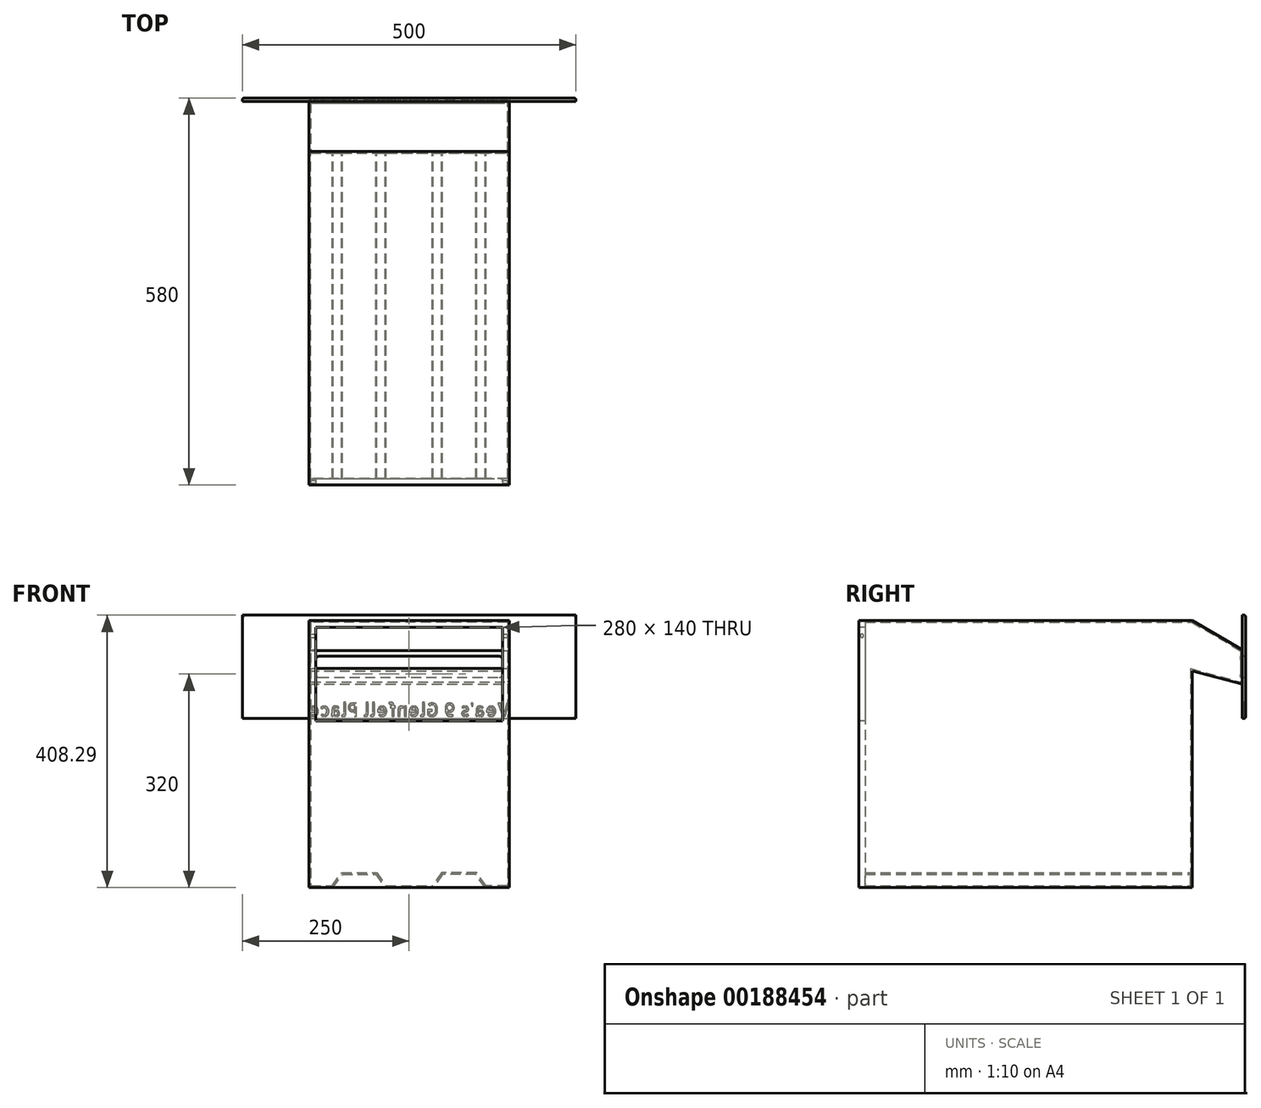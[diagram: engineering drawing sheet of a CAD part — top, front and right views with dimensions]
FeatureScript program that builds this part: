
annotation { "Feature Type Name" : "Feature", "Feature Type Description" : "" }
export const myFeature = defineFeature(function(context is Context, id is Id, definition is map)
    precondition{}
    {
        {
            var Q0;
            Q0=qCreatedBy(makeId("Front.planeOp"),FACE);
            var sketch = newSketch(context, id + "F0", { "sketchPlane" : qUnion([Q0])});
            skLineSegment(sketch, "E0", {"start": v(183.21, 0) * mm, "end": v(-199.24, 0) * mm, "construction": true});
            skLineSegment(sketch, "E1", {"start": v(0, -156.14) * mm, "end": v(0, 140.29) * mm, "construction": true});
            skLineSegment(sketch, "E2.right", {"start": v(150, 200) * mm, "end": v(150, -200) * mm});
            skPoint(sketch, "E2.middle", {"position": v(0, 0) * mm});
            skLineSegment(sketch, "E3", {"start": v(150, -200) * mm, "end": v(114, -200) * mm});
            skLineSegment(sketch, "E4", {"start": v(114, -200) * mm, "end": v(100, -180) * mm});
            skLineSegment(sketch, "E5", {"start": v(100, -180) * mm, "end": v(50, -180) * mm});
            skLineSegment(sketch, "E6", {"start": v(50, -180) * mm, "end": v(36, -200) * mm});
            skLineSegment(sketch, "E7", {"start": v(36, -200) * mm, "end": v(0, -200) * mm});
            skPoint(sketch, "E8", {"position": v(150, 0) * mm});
            skPoint(sketch, "E9", {"position": v(75, -180) * mm});
            skLineSegment(sketch, "E10", {"start": v(75, 0) * mm, "end": v(75, -200) * mm, "construction": true});
            skLineSegment(sketch, "E11", {"start": v(150, 200) * mm, "end": v(0, 200) * mm});
            skLineSegment(sketch, "E12.MirrorCS", {"start": v(-150, 200) * mm, "end": v(0, 200) * mm});
            skLineSegment(sketch, "E13.MirrorCS", {"start": v(-150, 200) * mm, "end": v(-150, -200) * mm});
            skLineSegment(sketch, "E14.MirrorCS", {"start": v(-150, -200) * mm, "end": v(-114, -200) * mm});
            skLineSegment(sketch, "E15.MirrorCS", {"start": v(-114, -200) * mm, "end": v(-100, -180) * mm});
            skLineSegment(sketch, "E16.MirrorCS", {"start": v(-100, -180) * mm, "end": v(-50, -180) * mm});
            skLineSegment(sketch, "E17.MirrorCS", {"start": v(-50, -180) * mm, "end": v(-36, -200) * mm});
            skLineSegment(sketch, "E18.MirrorCS", {"start": v(-36, -200) * mm, "end": v(0, -200) * mm});
            skSolve(sketch);
        }
        {
            var Q0;
            Q0 = qSketchRegion(id + "F0", true);
            extrude(context, id + "F1", {"entities" : qUnion([Q0]), "depth" : 500 * mm});
        }
        {
            var Q0;
            Q0=makeQuery(id+"F1.opExtrude","SWEPT_FACE",FACE,{"disambiguationData":[OSD([sQuery(id+"F0.wireOp",EDGE,"E2.right")])]});
            var sketch = newSketch(context, id + "F2", { "sketchPlane" : qUnion([Q0])});
            skLineSegment(sketch, "E19.0", {"start": v(0, 200) * mm, "end": v(0, -200) * mm, "construction": true});
            skLineSegment(sketch, "E20", {"start": v(0, 200) * mm, "end": v(75, 156.7) * mm});
            skLineSegment(sketch, "E21", {"start": v(0, 125) * mm, "end": v(75, 104.9) * mm});
            skLineSegment(sketch, "E22", {"start": v(75, 156.7) * mm, "end": v(75, 104.9) * mm});
            skLineSegment(sketch, "E23", {"start": v(0, 200) * mm, "end": v(0, 125) * mm});
            skSolve(sketch);
        }
        {
            var Q0;
            Q0 = qSketchRegion(id + "F2", true);
            var Q1;
            Q1=makeQuery(id+"F1.opExtrude","SWEPT_FACE",FACE,{"disambiguationData":[OSD([sQuery(id+"F0.wireOp",EDGE,"E13.MirrorCS")])]});
            var Q2;
            Q2=sQuery(id+"F0.wireOp",VERTEX,"E13.MirrorCS.start");
            extrude(context, id + "F3", {"entities" : qUnion([Q0]), "operationType" : NewBodyOperationType.ADD, "endBound" : BoundingType.UP_TO_SURFACE, "oppositeDirection" : true, "endBoundEntityFace" : qUnion([Q1]), "endBoundEntityVertex" : qUnion([Q2]), "depth" : 25 * mm});
        }
        {
            var Q0;
            Q0=makeQuery(id+"F1.opExtrude","CAP_FACE",FACE,{"disambiguationData":[OSD([sQuery(id+"F0.wireOp",EDGE,"E2.right"),sQuery(id+"F0.wireOp",EDGE,"E3"),sQuery(id+"F0.wireOp",EDGE,"E4"),sQuery(id+"F0.wireOp",EDGE,"E5"),sQuery(id+"F0.wireOp",EDGE,"E6"),sQuery(id+"F0.wireOp",EDGE,"E7"),sQuery(id+"F0.wireOp",EDGE,"E11"),sQuery(id+"F0.wireOp",EDGE,"E12.MirrorCS"),sQuery(id+"F0.wireOp",EDGE,"E13.MirrorCS"),sQuery(id+"F0.wireOp",EDGE,"E14.MirrorCS"),sQuery(id+"F0.wireOp",EDGE,"E15.MirrorCS"),sQuery(id+"F0.wireOp",EDGE,"E16.MirrorCS"),sQuery(id+"F0.wireOp",EDGE,"E17.MirrorCS"),sQuery(id+"F0.wireOp",EDGE,"E18.MirrorCS")])],"isStart":false});
            shell(context, id + "F4", {"entities" : qUnion([Q0]), "thickness" : 2.5 * mm});
        }
        {
            var Q0;
            Q0=makeQuery(id+"F3.opExtrude","SWEPT_FACE",FACE,{"disambiguationData":[OSD([sQuery(id+"F2.wireOp",EDGE,"E22")])]});
            var sketch = newSketch(context, id + "F5", { "sketchPlane" : qUnion([Q0])});
            skLineSegment(sketch, "E24.0", {"start": v(150, 156.7) * mm, "end": v(-150, 156.7) * mm, "construction": true});
            skLineSegment(sketch, "E24.1", {"start": v(-150, 156.7) * mm, "end": v(-150, 104.9) * mm, "construction": true});
            skLineSegment(sketch, "E24.2", {"start": v(150, 104.9) * mm, "end": v(-150, 104.9) * mm, "construction": true});
            skLineSegment(sketch, "E24.3", {"start": v(150, 104.9) * mm, "end": v(150, 156.7) * mm, "construction": true});
            skPoint(sketch, "E24.4", {"position": v(150, 130.8) * mm});
            skLineSegment(sketch, "E25.0", {"start": v(140, 119.9) * mm, "end": v(140, 141.7) * mm});
            skLineSegment(sketch, "E25.1", {"start": v(135, 114.9) * mm, "end": v(-135, 114.9) * mm});
            skLineSegment(sketch, "E25.2", {"start": v(-140, 141.7) * mm, "end": v(-140, 119.9) * mm});
            skLineSegment(sketch, "E25.3", {"start": v(135, 146.7) * mm, "end": v(-135, 146.7) * mm});
            skPoint(sketch, "E26.visualSharp", {"position": v(-140, 146.7) * mm});
            skArc(sketch, "E26.filletArc", {"start": v(-135, 146.7) * mm, "mid": v(-138.54, 145.23) * mm, "end": v(-140, 141.7) * mm});
            skPoint(sketch, "E27.visualSharp", {"position": v(-140, 114.9) * mm});
            skArc(sketch, "E27.filletArc", {"start": v(-140, 119.9) * mm, "mid": v(-138.54, 116.37) * mm, "end": v(-135, 114.9) * mm});
            skPoint(sketch, "E28.visualSharp", {"position": v(140, 114.9) * mm});
            skArc(sketch, "E28.filletArc", {"start": v(135, 114.9) * mm, "mid": v(138.54, 116.37) * mm, "end": v(140, 119.9) * mm});
            skPoint(sketch, "E29.visualSharp", {"position": v(140, 146.7) * mm});
            skArc(sketch, "E29.filletArc", {"start": v(140, 141.7) * mm, "mid": v(138.54, 145.23) * mm, "end": v(135, 146.7) * mm});
            skSolve(sketch);
        }
        {
            var Q0;
            Q0=makeQuery(id+"F5.imprint","IMPRINT",FACE,{"disambiguationData":[TD([[makeQuery(id+"F5.imprint","IMPRINT",EDGE,{"derivedFrom":sQuery(id+"F5.wireOp",EDGE,"E25.0")}),1.0]])]});
            extrude(context, id + "F6", {"entities" : qUnion([Q0]), "operationType" : NewBodyOperationType.REMOVE, "endBound" : BoundingType.UP_TO_NEXT, "oppositeDirection" : true, "depth" : 25 * mm});
        }
        {
            var Q0;
            Q0=makeQuery(id+"F1.opExtrude","CAP_FACE",FACE,{"disambiguationData":[OSD([sQuery(id+"F0.wireOp",EDGE,"E2.right"),sQuery(id+"F0.wireOp",EDGE,"E3"),sQuery(id+"F0.wireOp",EDGE,"E4"),sQuery(id+"F0.wireOp",EDGE,"E5"),sQuery(id+"F0.wireOp",EDGE,"E6"),sQuery(id+"F0.wireOp",EDGE,"E7"),sQuery(id+"F0.wireOp",EDGE,"E11"),sQuery(id+"F0.wireOp",EDGE,"E12.MirrorCS"),sQuery(id+"F0.wireOp",EDGE,"E13.MirrorCS"),sQuery(id+"F0.wireOp",EDGE,"E14.MirrorCS"),sQuery(id+"F0.wireOp",EDGE,"E15.MirrorCS"),sQuery(id+"F0.wireOp",EDGE,"E16.MirrorCS"),sQuery(id+"F0.wireOp",EDGE,"E17.MirrorCS"),sQuery(id+"F0.wireOp",EDGE,"E18.MirrorCS")])],"isStart":false});
            var sketch = newSketch(context, id + "F7", { "sketchPlane" : qUnion([Q0])});
            skLineSegment(sketch, "E30.0", {"start": v(-150, 200) * mm, "end": v(-150, -200) * mm});
            skLineSegment(sketch, "E30.10", {"start": v(150, 200) * mm, "end": v(150, -200) * mm});
            skLineSegment(sketch, "E30.11", {"start": v(150, 200) * mm, "end": v(-150, 200) * mm});
            skLineSegment(sketch, "E31.0", {"start": v(-140, 190) * mm, "end": v(-140, 50) * mm});
            skLineSegment(sketch, "E31.1", {"start": v(140, 190) * mm, "end": v(-140, 190) * mm});
            skLineSegment(sketch, "E31.2", {"start": v(140, 190) * mm, "end": v(140, 50) * mm});
            skLineSegment(sketch, "E32", {"start": v(-140, 50) * mm, "end": v(140, 50) * mm});
            skLineSegment(sketch, "E33", {"start": v(-150, -200) * mm, "end": v(150, -200) * mm});
            skSolve(sketch);
        }
        {
            var Q0;
            Q0 = qSketchRegion(id + "F7", true);
            extrude(context, id + "F8", {"entities" : qUnion([Q0]), "operationType" : NewBodyOperationType.ADD, "oppositeDirection" : true, "depth" : 10 * mm});
        }
        {
            var Q0;
            Q0=qCreatedBy(makeId("Right.planeOp"),FACE);
            var sketch = newSketch(context, id + "F9", { "sketchPlane" : qUnion([Q0])});
            skLineSegment(sketch, "E34.0.0", {"start": v(-500, 50) * mm, "end": v(-500, 190) * mm, "construction": true});
            skLineSegment(sketch, "E34.0.1", {"start": v(-500, 190) * mm, "end": v(-490, 190) * mm, "construction": true});
            skLineSegment(sketch, "E34.0.2", {"start": v(-490, 190) * mm, "end": v(-490, 50) * mm, "construction": true});
            skLineSegment(sketch, "E34.0.3", {"start": v(-490, 50) * mm, "end": v(-500, 50) * mm, "construction": true});
            skCircle(sketch, "E35", {"center": v(-495, 177.5) * mm, "radius": 2.5 * mm});
            skLineSegment(sketch, "E36", {"start": v(-495, 177.5) * mm, "end": v(-495, 190) * mm, "construction": true});
            skSolve(sketch);
        }
        {
            var Q0;
            Q0=makeQuery(id+"F9.imprint","IMPRINT",FACE,{"disambiguationData":[TD([[makeQuery(id+"F9.imprint","IMPRINT",EDGE,{"derivedFrom":sQuery(id+"F9.wireOp",EDGE,"E35")}),1.0]])]});
            var Q1;
            Q1=makeQuery(id+"F3.boolean.opBoolean","MERGE",FACE,{"derivedFrom":[makeQuery(id+"F1.opExtrude","SWEPT_FACE",FACE,{"disambiguationData":[OSD([sQuery(id+"F0.wireOp",EDGE,"E2.right")])]}),makeQuery(id+"F3.opExtrude","CAP_FACE",FACE,{"disambiguationData":[OSD([sQuery(id+"F2.wireOp",EDGE,"E20"),sQuery(id+"F2.wireOp",EDGE,"E21"),sQuery(id+"F2.wireOp",EDGE,"E22"),sQuery(id+"F2.wireOp",EDGE,"E23")])],"isStart":true})]});
            extrude(context, id + "F10", {"entities" : qUnion([Q0]), "operationType" : NewBodyOperationType.REMOVE, "oppositeDirection" : true, "depth" : 295 * mm, "hasSecondDirection" : true, "secondDirectionBound" : BoundingType.UP_TO_SURFACE, "secondDirectionOppositeDirection" : false, "secondDirectionBoundEntityFace" : qUnion([Q1]), "secondDirectionDepth" : 25 * mm, "symmetric" : true});
        }
        {
            var Q0;
            Q0=makeQuery(id+"F3.opExtrude","SWEPT_FACE",FACE,{"disambiguationData":[OSD([sQuery(id+"F2.wireOp",EDGE,"E22")])]});
            var sketch = newSketch(context, id + "F11", { "sketchPlane" : qUnion([Q0])});
            skLineSegment(sketch, "E37.0", {"start": v(135, 114.9) * mm, "end": v(-135, 114.9) * mm});
            skArc(sketch, "E37.1", {"start": v(-140, 119.9) * mm, "mid": v(-138.54, 116.37) * mm, "end": v(-135, 114.9) * mm});
            skLineSegment(sketch, "E37.2", {"start": v(-140, 141.7) * mm, "end": v(-140, 119.9) * mm});
            skArc(sketch, "E37.3", {"start": v(-135, 146.7) * mm, "mid": v(-138.54, 145.23) * mm, "end": v(-140, 141.7) * mm});
            skLineSegment(sketch, "E37.4", {"start": v(135, 146.7) * mm, "end": v(-135, 146.7) * mm});
            skArc(sketch, "E37.5", {"start": v(140, 141.7) * mm, "mid": v(138.54, 145.23) * mm, "end": v(135, 146.7) * mm});
            skLineSegment(sketch, "E37.6", {"start": v(140, 119.9) * mm, "end": v(140, 141.7) * mm});
            skArc(sketch, "E37.7", {"start": v(135, 114.9) * mm, "mid": v(138.54, 116.37) * mm, "end": v(140, 119.9) * mm});
            skLineSegment(sketch, "E38", {"start": v(0, 146.7) * mm, "end": v(0, 114.9) * mm, "construction": true});
            skPoint(sketch, "E39", {"position": v(0, 130.8) * mm});
            skLineSegment(sketch, "E40.bottom", {"start": v(250, 53.32) * mm, "end": v(-250, 53.32) * mm});
            skLineSegment(sketch, "E40.top", {"start": v(250, 208.29) * mm, "end": v(-250, 208.29) * mm});
            skLineSegment(sketch, "E40.left", {"start": v(250, 53.32) * mm, "end": v(250, 208.29) * mm});
            skLineSegment(sketch, "E40.right", {"start": v(-250, 53.32) * mm, "end": v(-250, 208.29) * mm});
            skLineSegment(sketch, "E41.0", {"start": v(150, 156.7) * mm, "end": v(-150, 156.7) * mm, "construction": true});
            skLineSegment(sketch, "E42", {"start": v(-151.77, 166.7) * mm, "end": v(151.77, 166.7) * mm, "construction": true});
            skPoint(sketch, "E43", {"position": v(0, 166.7) * mm});
            skText(sketch, "E44", { "text": "Vea\'s 9 Glenfell Place", "fontName": "AllertaStencil-Regular.ttf"});
            const initialGuessF11  = {"E44": [-0.15177, 0.0567, 1, 0, 0.0198]};
            skSetInitialGuess(sketch, initialGuessF11);
            skSolve(sketch);
        }
        {
            var Q0;
            Q0 = qSketchRegion(id + "F11", true);
            extrude(context, id + "F12", {"entities" : qUnion([Q0]), "operationType" : NewBodyOperationType.ADD, "depth" : 5 * mm});
        }
        {
            var Q0;
            Q0=makeQuery(id+"F12.opExtrude","CAP_EDGE",EDGE,{"disambiguationData":[OSD([sQuery(id+"F11.wireOp",EDGE,"E37.0")])],"isStart":false});
            var Q1;
            Q1=makeQuery(id+"F12.opExtrude","CAP_EDGE",EDGE,{"disambiguationData":[OSD([sQuery(id+"F11.wireOp",EDGE,"E40.left")])],"isStart":false});
            var Q2;
            Q2=makeQuery(id+"F12.opExtrude","CAP_EDGE",EDGE,{"disambiguationData":[OSD([sQuery(id+"F11.wireOp",EDGE,"E40.bottom")])],"isStart":false});
            var Q3;
            Q3=makeQuery(id+"F12.opExtrude","CAP_EDGE",EDGE,{"disambiguationData":[OSD([sQuery(id+"F11.wireOp",EDGE,"E40.top")])],"isStart":false});
            var Q4;
            Q4=makeQuery(id+"F12.opExtrude","CAP_EDGE",EDGE,{"disambiguationData":[OSD([sQuery(id+"F11.wireOp",EDGE,"E40.right")])],"isStart":false});
            fillet(context, id + "F13", {"entities" : qUnion([Q0, Q1, Q2, Q3, Q4]), "radius" : 2.5 * mm, "tangentPropagation" : true, "allowEdgeOverflow" : false});
        }
    });
